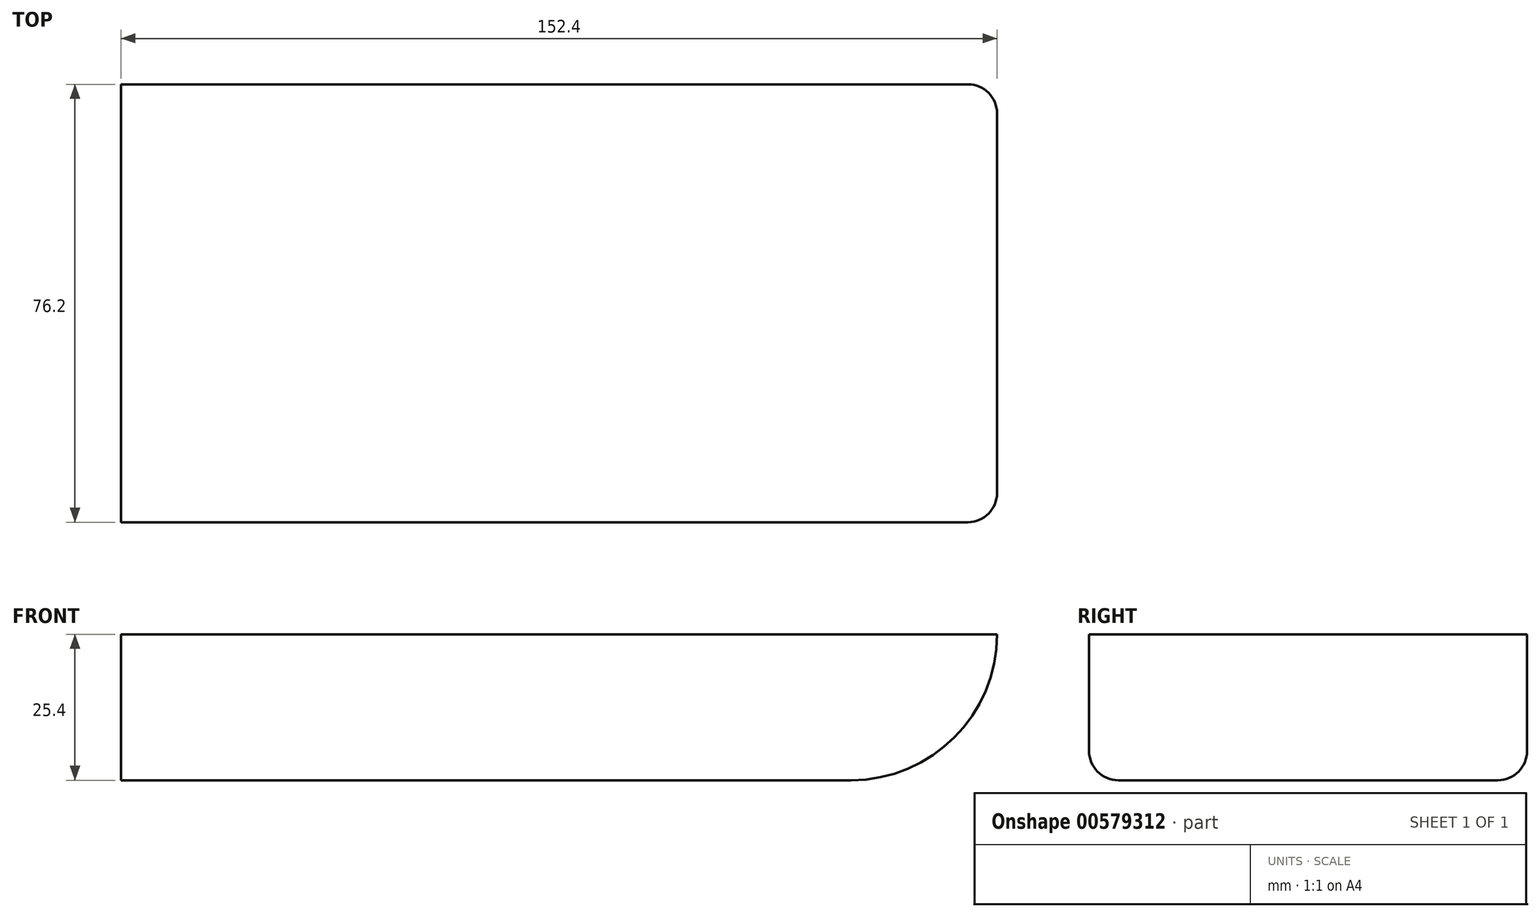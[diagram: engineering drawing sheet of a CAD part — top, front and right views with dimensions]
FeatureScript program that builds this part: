
annotation { "Feature Type Name" : "Feature", "Feature Type Description" : "" }
export const myFeature = defineFeature(function(context is Context, id is Id, definition is map)
    precondition{}
    {
        {
            var Q0;
            Q0=qCreatedBy(makeId("Front.planeOp"),FACE);
            var sketch = newSketch(context, id + "F0", { "sketchPlane" : qUnion([Q0])});
            skLineSegment(sketch, "E0.bottom", {"start": v(63.5, 12.7) * mm, "end": v(-63.5, 12.7) * mm});
            skLineSegment(sketch, "E0.top", {"start": v(63.5, -12.7) * mm, "end": v(-63.5, -12.7) * mm});
            skLineSegment(sketch, "E0.left", {"start": v(63.5, 12.7) * mm, "end": v(63.5, -12.7) * mm});
            skLineSegment(sketch, "E0.right", {"start": v(-63.5, 12.7) * mm, "end": v(-63.5, -12.7) * mm});
            skPoint(sketch, "E0.middle", {"position": v(0, 0) * mm});
            skLineSegment(sketch, "E1", {"start": v(63.5, 12.7) * mm, "end": v(88.9, 12.7) * mm});
            skArc(sketch, "E2", {"start": v(63.5, -12.7) * mm, "mid": v(81.46, -5.26) * mm, "end": v(88.9, 12.7) * mm});
            skSolve(sketch);
        }
        {
            var Q0;
            Q0=makeQuery(id+"F0.imprint","IMPRINT",FACE,{"disambiguationData":[TD([[makeQuery(id+"F0.imprint","IMPRINT",EDGE,{"derivedFrom":sQuery(id+"F0.wireOp",EDGE,"E0.bottom")}),1.0]])]});
            var Q1;
            Q1=makeQuery(id+"F0.imprint","IMPRINT",FACE,{"disambiguationData":[TD([[makeQuery(id+"F0.imprint","IMPRINT",EDGE,{"derivedFrom":sQuery(id+"F0.wireOp",EDGE,"E0.left")}),1.0]])]});
            extrude(context, id + "F1", {"entities" : qUnion([Q0, Q1]), "depth" : 76.2 * mm, "offsetDistance" : 25.4 * mm});
        }
        {
            var Q0;
            Q0=makeQuery(id+"F1.opExtrude","CAP_EDGE",EDGE,{"disambiguationData":[OSD([sQuery(id+"F0.wireOp",EDGE,"E0.top")])],"isStart":false});
            var Q1;
            Q1=makeQuery(id+"F1.opExtrude","CAP_EDGE",EDGE,{"disambiguationData":[OSD([sQuery(id+"F0.wireOp",EDGE,"E0.top")])],"isStart":true});
            fillet(context, id + "F2", {"entities" : qUnion([Q0, Q1]), "radius" : 5.08 * mm, "tangentPropagation" : true, "allowEdgeOverflow" : false});
        }
    });
